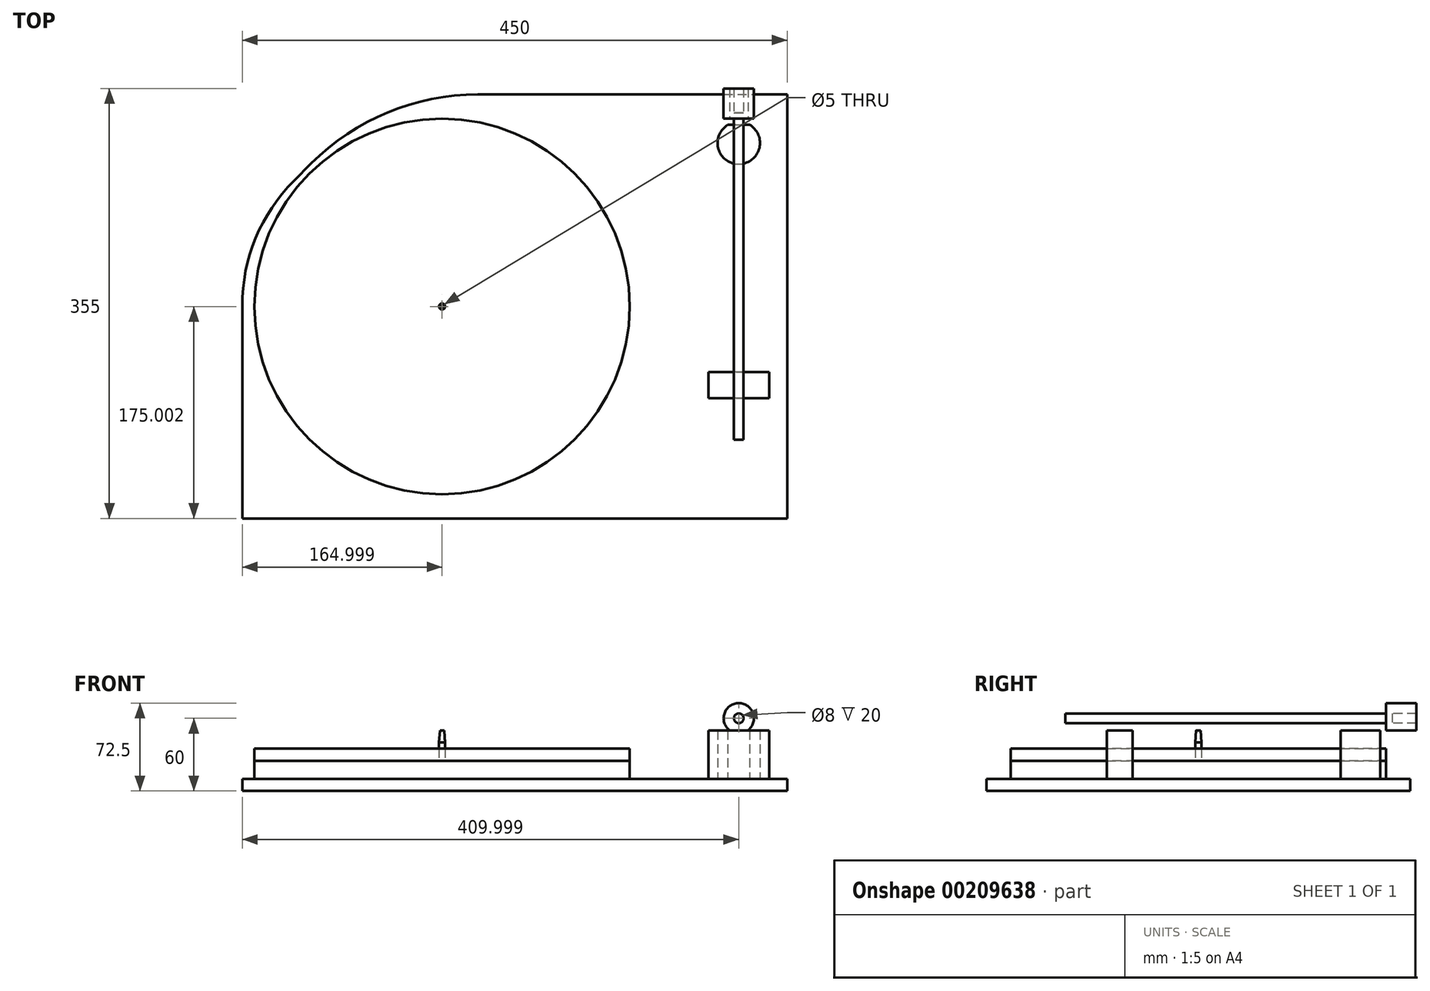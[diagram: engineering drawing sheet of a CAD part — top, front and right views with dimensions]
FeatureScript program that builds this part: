
annotation { "Feature Type Name" : "Feature", "Feature Type Description" : "" }
export const myFeature = defineFeature(function(context is Context, id is Id, definition is map)
    precondition{}
    {
        {
            var Q0;
            Q0=qCreatedBy(makeId("Top.planeOp"),FACE);
            var sketch = newSketch(context, id + "F0", { "sketchPlane" : qUnion([Q0])});
            skLineSegment(sketch, "E0.bottom", {"start": v(52.57, 399.5) * mm, "end": v(502.57, 399.5) * mm});
            skLineSegment(sketch, "E0.top", {"start": v(52.57, 49.5) * mm, "end": v(502.57, 49.5) * mm});
            skLineSegment(sketch, "E0.left", {"start": v(52.57, 399.5) * mm, "end": v(52.57, 49.5) * mm});
            skLineSegment(sketch, "E0.right", {"start": v(502.57, 399.5) * mm, "end": v(502.57, 49.5) * mm});
            skCircle(sketch, "E1", {"center": v(217.57, 224.5) * mm, "radius": 155 * mm});
            skPoint(sketch, "E1.centerSnap0", {"position": v(52.57, 224.5) * mm});
            skArc(sketch, "E2", {"start": v(453.55, 374.5) * mm, "mid": v(462.57, 342) * mm, "end": v(471.58, 374.5) * mm});
            skLineSegment(sketch, "E3.bottom", {"start": v(487.76, 170.25) * mm, "end": v(437.37, 170.25) * mm});
            skLineSegment(sketch, "E3.top", {"start": v(487.76, 148.75) * mm, "end": v(437.37, 148.75) * mm});
            skLineSegment(sketch, "E3.left", {"start": v(487.76, 170.25) * mm, "end": v(487.76, 148.75) * mm});
            skLineSegment(sketch, "E3.right", {"start": v(437.37, 170.25) * mm, "end": v(437.37, 148.75) * mm});
            skPoint(sketch, "E3.middle", {"position": v(462.57, 159.5) * mm});
            skLineSegment(sketch, "E4", {"start": v(453.55, 374.5) * mm, "end": v(471.58, 374.5) * mm});
            skCircle(sketch, "E5", {"center": v(217.57, 224.5) * mm, "radius": 2.5 * mm});
            skLineSegment(sketch, "E6.0", {"start": v(12.57, 439.5) * mm, "end": v(542.57, 439.5) * mm, "construction": true});
            skLineSegment(sketch, "E6.1", {"start": v(12.57, 439.5) * mm, "end": v(12.57, 9.5) * mm, "construction": true});
            skLineSegment(sketch, "E6.2", {"start": v(12.57, 9.5) * mm, "end": v(542.57, 9.5) * mm, "construction": true});
            skLineSegment(sketch, "E6.3", {"start": v(542.57, 439.5) * mm, "end": v(542.57, 9.5) * mm, "construction": true});
            skLineSegment(sketch, "E7.0", {"start": v(62.57, 389.5) * mm, "end": v(492.57, 389.5) * mm, "construction": true});
            skLineSegment(sketch, "E7.1", {"start": v(62.57, 389.5) * mm, "end": v(62.57, 59.5) * mm, "construction": true});
            skLineSegment(sketch, "E7.2", {"start": v(62.57, 59.5) * mm, "end": v(492.57, 59.5) * mm, "construction": true});
            skLineSegment(sketch, "E7.3", {"start": v(492.57, 389.5) * mm, "end": v(492.57, 59.5) * mm, "construction": true});
            skLineSegment(sketch, "E8.bottom", {"start": v(62.57, 389.5) * mm, "end": v(12.57, 389.5) * mm});
            skLineSegment(sketch, "E8.top", {"start": v(62.57, 439.5) * mm, "end": v(12.57, 439.5) * mm});
            skLineSegment(sketch, "E8.left", {"start": v(62.57, 389.5) * mm, "end": v(62.57, 439.5) * mm});
            skLineSegment(sketch, "E8.right", {"start": v(12.57, 389.5) * mm, "end": v(12.57, 439.5) * mm});
            skLineSegment(sketch, "E9.bottom", {"start": v(492.57, 389.5) * mm, "end": v(542.57, 389.5) * mm});
            skLineSegment(sketch, "E9.top", {"start": v(492.57, 439.5) * mm, "end": v(542.57, 439.5) * mm});
            skLineSegment(sketch, "E9.left", {"start": v(492.57, 389.5) * mm, "end": v(492.57, 439.5) * mm});
            skLineSegment(sketch, "E9.right", {"start": v(542.57, 389.5) * mm, "end": v(542.57, 439.5) * mm});
            skLineSegment(sketch, "E10.bottom", {"start": v(492.57, 59.5) * mm, "end": v(542.57, 59.5) * mm});
            skLineSegment(sketch, "E10.top", {"start": v(492.57, 9.5) * mm, "end": v(542.57, 9.5) * mm});
            skLineSegment(sketch, "E10.left", {"start": v(492.57, 59.5) * mm, "end": v(492.57, 9.5) * mm});
            skLineSegment(sketch, "E10.right", {"start": v(542.57, 59.5) * mm, "end": v(542.57, 9.5) * mm});
            skLineSegment(sketch, "E11.bottom", {"start": v(62.57, 59.5) * mm, "end": v(12.57, 59.5) * mm});
            skLineSegment(sketch, "E11.top", {"start": v(62.57, 9.5) * mm, "end": v(12.57, 9.5) * mm});
            skLineSegment(sketch, "E11.left", {"start": v(62.57, 59.5) * mm, "end": v(62.57, 9.5) * mm});
            skLineSegment(sketch, "E11.right", {"start": v(12.57, 59.5) * mm, "end": v(12.57, 9.5) * mm});
            skCircle(sketch, "E12", {"center": v(37.57, 414.5) * mm, "radius": 10 * mm});
            skPoint(sketch, "E12.centerSnap0", {"position": v(37.57, 439.5) * mm});
            skPoint(sketch, "E12.centerSnap1", {"position": v(12.57, 414.5) * mm});
            skCircle(sketch, "E13", {"center": v(517.57, 414.5) * mm, "radius": 10 * mm});
            skPoint(sketch, "E13.centerSnap0", {"position": v(517.57, 389.5) * mm});
            skPoint(sketch, "E13.centerSnap1", {"position": v(492.57, 414.5) * mm});
            skCircle(sketch, "E14", {"center": v(517.57, 34.5) * mm, "radius": 10 * mm});
            skPoint(sketch, "E14.centerSnap0", {"position": v(542.57, 34.5) * mm});
            skPoint(sketch, "E14.centerSnap1", {"position": v(517.57, 59.5) * mm});
            skCircle(sketch, "E15", {"center": v(37.57, 34.5) * mm, "radius": 10 * mm});
            skPoint(sketch, "E15.centerSnap0", {"position": v(37.57, 9.5) * mm});
            skPoint(sketch, "E15.centerSnap1", {"position": v(12.57, 34.5) * mm});
            skPoint(sketch, "E16", {"position": v(217.57, 399.5) * mm});
            skSolve(sketch);
        }
        {
            var Q0;
            Q0=makeQuery(id+"F0.imprint","IMPRINT",FACE,{"disambiguationData":[TD([[makeQuery(id+"F0.imprint","IMPRINT",EDGE,{"derivedFrom":sQuery(id+"F0.wireOp",EDGE,"E1")}),1.0]])]});
            var Q1;
            Q1=makeQuery(id+"F0.imprint","IMPRINT",FACE,{"disambiguationData":[TD([[makeQuery(id+"F0.imprint","IMPRINT",EDGE,{"derivedFrom":sQuery(id+"F0.wireOp",EDGE,"E0.bottom")}),-1.0]])]});
            var Q2;
            Q2=makeQuery(id+"F0.imprint","IMPRINT",FACE,{"disambiguationData":[TD([[makeQuery(id+"F0.imprint","IMPRINT",EDGE,{"derivedFrom":sQuery(id+"F0.wireOp",EDGE,"E2")}),1.0]])]});
            var Q3;
            Q3=makeQuery(id+"F0.imprint","IMPRINT",FACE,{"disambiguationData":[TD([[makeQuery(id+"F0.imprint","IMPRINT",EDGE,{"derivedFrom":sQuery(id+"F0.wireOp",EDGE,"E3.bottom")}),1.0]])]});
            var Q4;
            Q4=makeQuery(id+"F0.imprint","IMPRINT",FACE,{"disambiguationData":[TD([[makeQuery(id+"F0.imprint","IMPRINT",EDGE,{"derivedFrom":sQuery(id+"F0.wireOp",EDGE,"E1")}),-1.0]])]});
            var Q5;
            {var subQ0=sQuery(id+"F0.wireOp",EDGE,"E0.left");var subQ1=sQuery(id+"F0.wireOp",EDGE,"E0.top");var subQ2=makeQuery(id+"F0.imprint","INTERSECT",VERTEX,{"derivedFrom":[subQ1,subQ0]});Q5=makeQuery(id+"F0.imprint","IMPRINT",FACE,{"disambiguationData":[TD([[makeQuery(id+"F0.imprint","IMPRINT",EDGE,{"disambiguationData":[TD([[subQ2,-1.0]])],"derivedFrom":subQ1}),1.0]])]});}
            var Q6;
            {var subQ0=sQuery(id+"F0.wireOp",EDGE,"E0.right");var subQ1=sQuery(id+"F0.wireOp",EDGE,"E0.top");var subQ2=makeQuery(id+"F0.imprint","INTERSECT",VERTEX,{"derivedFrom":[subQ1,subQ0]});Q6=makeQuery(id+"F0.imprint","IMPRINT",FACE,{"disambiguationData":[TD([[makeQuery(id+"F0.imprint","IMPRINT",EDGE,{"disambiguationData":[TD([[subQ2,1.0]])],"derivedFrom":subQ1}),1.0]])]});}
            extrude(context, id + "F1", {"entities" : qUnion([Q0, Q1, Q2, Q3, Q4, Q5, Q6]), "depth" : 10 * mm});
        }
        {
            var Q0;
            Q0=makeQuery(id+"F0.imprint","IMPRINT",FACE,{"disambiguationData":[TD([[makeQuery(id+"F0.imprint","IMPRINT",EDGE,{"derivedFrom":sQuery(id+"F0.wireOp",EDGE,"E2")}),1.0]])]});
            var Q1;
            Q1=makeQuery(id+"F0.imprint","IMPRINT",FACE,{"disambiguationData":[TD([[makeQuery(id+"F0.imprint","IMPRINT",EDGE,{"derivedFrom":sQuery(id+"F0.wireOp",EDGE,"E3.bottom")}),1.0]])]});
            var Q2;
            Q2=makeQuery(id+"F0.imprint","IMPRINT",FACE,{"disambiguationData":[TD([[makeQuery(id+"F0.imprint","IMPRINT",EDGE,{"derivedFrom":sQuery(id+"F0.wireOp",EDGE,"E1")}),1.0]])]});
            extrude(context, id + "F2", {"entities" : qUnion([Q0, Q1, Q2]), "operationType" : NewBodyOperationType.ADD, "depth" : 25 * mm});
        }
        {
            var Q0;
            Q0=makeQuery(id+"F2.opExtrude","CAP_FACE",FACE,{"disambiguationData":[OSD([sQuery(id+"F0.wireOp",EDGE,"E2"),sQuery(id+"F0.wireOp",EDGE,"E4")])],"isStart":false});
            var Q1;
            Q1=makeQuery(id+"F2.opExtrude","CAP_FACE",FACE,{"disambiguationData":[OSD([sQuery(id+"F0.wireOp",EDGE,"E3.bottom"),sQuery(id+"F0.wireOp",EDGE,"E3.top"),sQuery(id+"F0.wireOp",EDGE,"E3.left"),sQuery(id+"F0.wireOp",EDGE,"E3.right")])],"isStart":false});
            extrude(context, id + "F3", {"entities" : qUnion([Q0, Q1]), "operationType" : NewBodyOperationType.ADD, "depth" : 25 * mm});
        }
        {
            var Q0;
            Q0=makeQuery(id+"F2.opExtrude","SWEPT_FACE",FACE,{"disambiguationData":[OSD([sQuery(id+"F0.wireOp",EDGE,"E4")])]});
            var sketch = newSketch(context, id + "F4", { "sketchPlane" : qUnion([Q0])});
            skCircle(sketch, "E17", {"center": v(-462.57, 60) * mm, "radius": 4 * mm});
            skPoint(sketch, "E18", {"position": v(-462.57, 50) * mm});
            skCircle(sketch, "E19", {"center": v(-462.57, 60) * mm, "radius": 12.5 * mm});
            skSolve(sketch);
        }
        {
            var Q0;
            Q0=makeQuery(id+"F4.imprint","IMPRINT",FACE,{"disambiguationData":[TD([[makeQuery(id+"F4.imprint","IMPRINT",EDGE,{"derivedFrom":sQuery(id+"F4.wireOp",EDGE,"E17")}),-1.0]])]});
            extrude(context, id + "F5", {"entities" : qUnion([Q0]), "depth" : 30 * mm, "hasSecondDirection" : true, "secondDirectionOppositeDirection" : false, "secondDirectionDepth" : 5 * mm});
        }
        {
            var Q0;
            Q0=makeQuery(id+"F4.imprint","IMPRINT",FACE,{"disambiguationData":[TD([[makeQuery(id+"F4.imprint","IMPRINT",EDGE,{"derivedFrom":sQuery(id+"F4.wireOp",EDGE,"E17")}),1.0]])]});
            extrude(context, id + "F6", {"entities" : qUnion([Q0]), "operationType" : NewBodyOperationType.ADD, "oppositeDirection" : true, "depth" : 260 * mm, "hasSecondDirection" : true, "secondDirectionOppositeDirection" : false, "secondDirectionDepth" : 10 * mm});
        }
        {
            var Q0;
            Q0=makeQuery(id+"F0.imprint","IMPRINT",FACE,{"disambiguationData":[TD([[makeQuery(id+"F0.imprint","IMPRINT",EDGE,{"derivedFrom":sQuery(id+"F0.wireOp",EDGE,"E5")}),1.0]])]});
            extrude(context, id + "F7", {"entities" : qUnion([Q0]), "operationType" : NewBodyOperationType.ADD, "depth" : 40 * mm});
        }
        {
            var Q0;
            Q0=makeQuery(id+"F7.opExtrude","CAP_FACE",FACE,{"disambiguationData":[OSD([sQuery(id+"F0.wireOp",EDGE,"E5")])],"isStart":false});
            extrude(context, id + "F8", {"entities" : qUnion([Q0]), "operationType" : NewBodyOperationType.ADD, "depth" : 10 * mm, "hasDraft" : true, "draftAngle" : 4 * degree, "draftPullDirection" : true});
        }
        {
            var Q0;
            Q0=makeQuery(id+"F1.opExtrude","SWEPT_EDGE",EDGE,{"disambiguationData":[OSD([sQuery(id+"F0.wireOp",EDGE,"E0.bottom"),sQuery(id+"F0.wireOp",EDGE,"E0.left")])]});
            chamfer(context, id + "F9", {"entities" : qUnion([Q0]), "width" : 114 * mm, "tangentPropagation" : true});
        }
        {
            var Q0;
            {var subQ0=sQuery(id+"F0.wireOp",EDGE,"E0.left");Q0=makeQuery(id+"F9.opChamfer","BLEND_EDGE",EDGE,{"blendedFrom":[makeQuery(id+"F1.opExtrude","SWEPT_EDGE",EDGE,{"disambiguationData":[OSD([sQuery(id+"F0.wireOp",EDGE,"E0.bottom"),subQ0])]}),makeQuery(id+"F1.opExtrude","SWEPT_FACE",FACE,{"disambiguationData":[OSD([subQ0])]})],"blendedInto":[makeQuery(id+"F1.opExtrude","SWEPT_FACE",FACE,{"disambiguationData":[OSD([subQ0])]})]});}
            fillet(context, id + "F10", {"entities" : qUnion([Q0]), "radius" : 145.64 * mm, "tangentPropagation" : true, "allowEdgeOverflow" : false});
        }
        {
            var Q0;
            {var subQ0=sQuery(id+"F0.wireOp",EDGE,"E0.bottom");Q0=makeQuery(id+"F9.opChamfer","BLEND_EDGE",EDGE,{"blendedFrom":[makeQuery(id+"F1.opExtrude","SWEPT_EDGE",EDGE,{"disambiguationData":[OSD([subQ0,sQuery(id+"F0.wireOp",EDGE,"E0.left")])]}),makeQuery(id+"F1.opExtrude","SWEPT_FACE",FACE,{"disambiguationData":[OSD([subQ0])]})],"blendedInto":[makeQuery(id+"F1.opExtrude","SWEPT_FACE",FACE,{"disambiguationData":[OSD([subQ0])]})]});}
            fillet(context, id + "F11", {"entities" : qUnion([Q0]), "radius" : 194.2 * mm, "tangentPropagation" : true, "allowEdgeOverflow" : false});
        }
        {
            var Q0;
            Q0=makeQuery(id+"F2.opExtrude","CAP_FACE",FACE,{"disambiguationData":[OSD([sQuery(id+"F0.wireOp",EDGE,"E1"),sQuery(id+"F0.wireOp",EDGE,"E5")])],"isStart":false});
            extrude(context, id + "F12", {"entities" : qUnion([Q0]), "depth" : 10 * mm});
        }
    });
